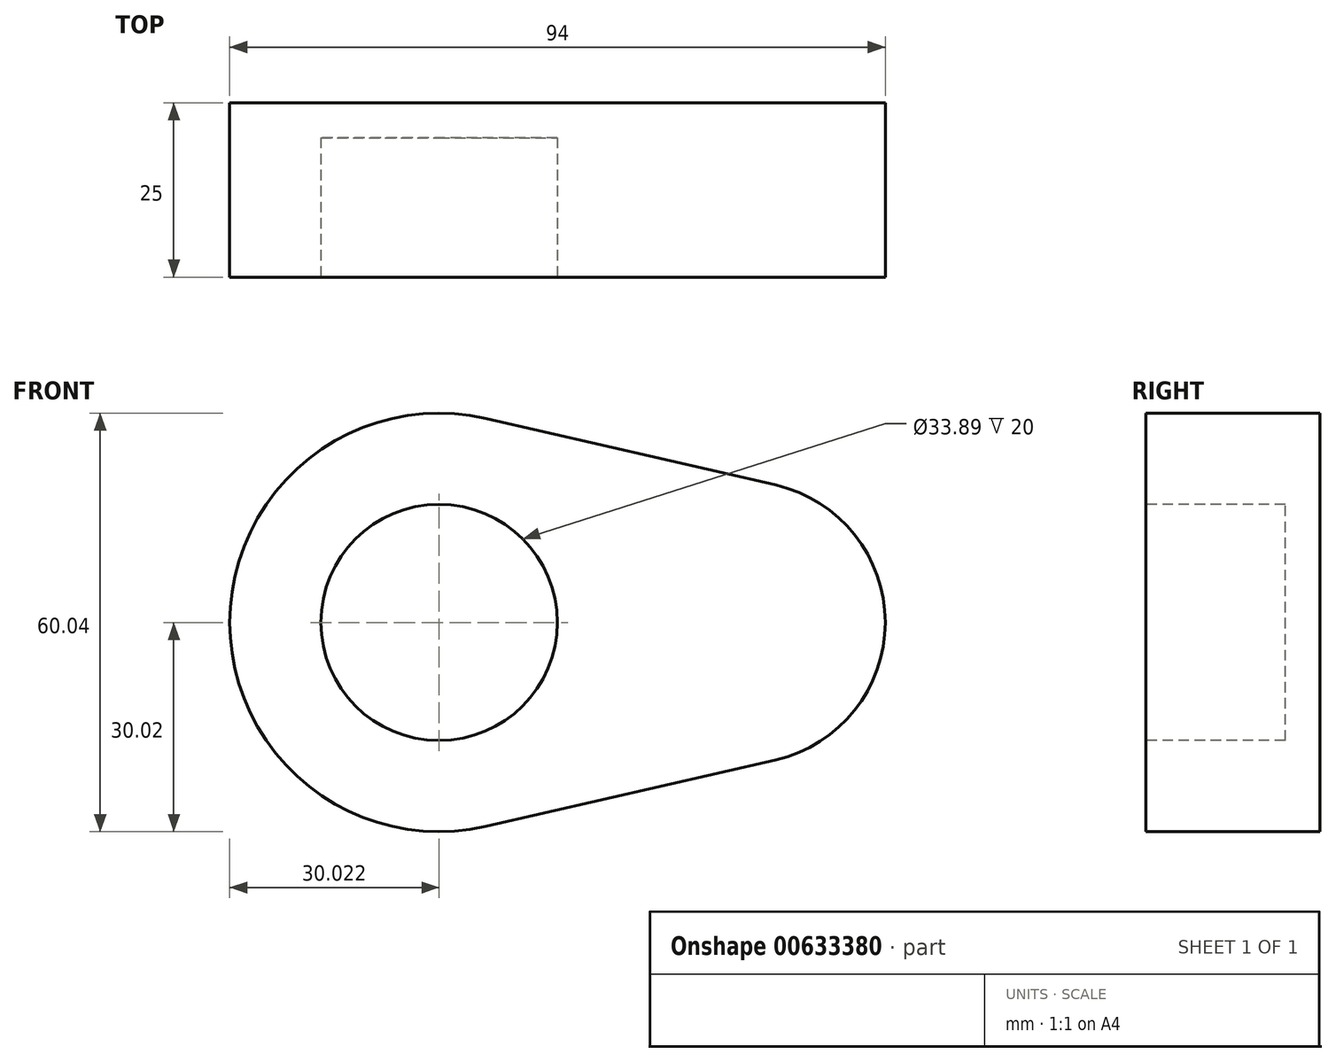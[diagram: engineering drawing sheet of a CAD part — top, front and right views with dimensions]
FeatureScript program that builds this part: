
annotation { "Feature Type Name" : "Feature", "Feature Type Description" : "" }
export const myFeature = defineFeature(function(context is Context, id is Id, definition is map)
    precondition{}
    {
        {
            var Q0;
            Q0=qCreatedBy(makeId("Front.planeOp"),FACE);
            var sketch = newSketch(context, id + "F0", { "sketchPlane" : qUnion([Q0])});
            skArc(sketch, "E0", {"start": v(-16.55, 29.26) * mm, "mid": v(-53.3, 0) * mm, "end": v(-16.55, -29.26) * mm});
            skArc(sketch, "E1", {"start": v(25, 19.7) * mm, "mid": v(40.7, 0) * mm, "end": v(25, -19.7) * mm});
            skLineSegment(sketch, "E2", {"start": v(-16.55, 29.26) * mm, "end": v(25, 19.7) * mm});
            skLineSegment(sketch, "E3", {"start": v(25, -19.7) * mm, "end": v(-16.55, -29.26) * mm});
            skSolve(sketch);
        }
        {
            var Q0;
            Q0=makeQuery(id+"F0.imprint","IMPRINT",FACE,{"disambiguationData":[TD([[makeQuery(id+"F0.imprint","IMPRINT",EDGE,{"derivedFrom":sQuery(id+"F0.wireOp",EDGE,"E0")}),1.0]])]});
            extrude(context, id + "F1", {"entities" : qUnion([Q0]), "oppositeDirection" : true, "depth" : 25 * mm, "offsetDistance" : 25 * mm});
        }
        {
            var Q0;
            Q0=makeQuery(id+"F1.opExtrude","CAP_FACE",FACE,{"disambiguationData":[OSD([sQuery(id+"F0.wireOp",EDGE,"E0"),sQuery(id+"F0.wireOp",EDGE,"E1"),sQuery(id+"F0.wireOp",EDGE,"E2"),sQuery(id+"F0.wireOp",EDGE,"E3")])],"isStart":true});
            var sketch = newSketch(context, id + "F2", { "sketchPlane" : qUnion([Q0])});
            skCircle(sketch, "E4", {"center": v(20.48, 0) * mm, "radius": 11.39 * mm});
            skCircle(sketch, "E5", {"center": v(-23.28, 0) * mm, "radius": 16.94 * mm});
            skSolve(sketch);
        }
        {
            var Q0;
            Q0=makeQuery(id+"F2.imprint","IMPRINT",FACE,{"disambiguationData":[TD([[makeQuery(id+"F2.imprint","IMPRINT",EDGE,{"derivedFrom":sQuery(id+"F2.wireOp",EDGE,"E5")}),1.0]])]});
            var Q1;
            Q1=sQuery(id+"F2.wireOp",EDGE,"E5");
            extrude(context, id + "F3", {"entities" : qUnion([Q0]), "operationType" : NewBodyOperationType.REMOVE, "surfaceEntities" : qUnion([Q1]), "oppositeDirection" : true, "depth" : 20 * mm, "offsetDistance" : 25 * mm});
        }
    });
